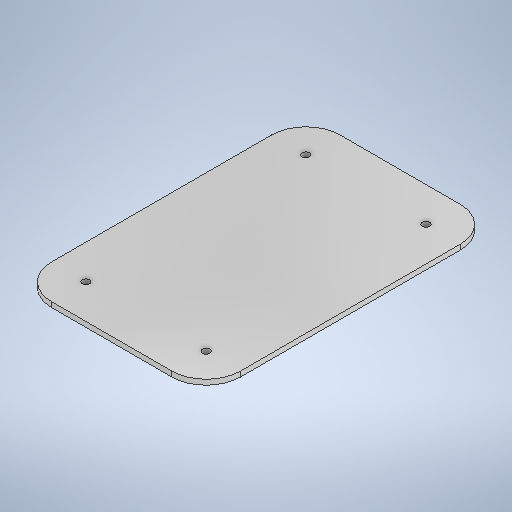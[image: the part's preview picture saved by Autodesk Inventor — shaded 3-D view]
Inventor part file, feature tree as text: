
AUTODESK INVENTOR PART (.ipt)
format: ipt  version: 2025.2 (Build 292293000, 293)  size: 270,848 bytes
history: native  units: mm
features: sketch x2, plane x2, extrude x1, fillet x1, hole x1
ambient origin geometry x8: Origin, YZ Plane, XZ Plane, XY Plane, X Axis, Y Axis, Z Axis, Center Point
bodies: Solid1 (feature_tree)
feature tree (7):
  sketch  "Sketch1"  dims[d4=110.0mm d5=168.0mm d20=3.0mm d21=0.0mm]
  extrude  "Extrusion2"  Depth=168.0mm
  fillet  "Fillet1"  Radius=3.0mm
  plane  "Work Plane1"
  plane  "Work Plane2"
  hole  "Hole2"  [1 undecoded]
  sketch  "Sketch2"  dims[d22=5.0mm d23=18.0mm d24=24.0mm d25=5.0mm d26=18.0mm d27=24.0mm d35=20.0mm d36=-84.0mm d37=-55.0mm d38=4.3mm d39=6.0mm d40=4.0mm d41=2.0mm d42=90.0deg d43=8.0mm d44=20.594885mm]
note: 1 required parameter value undecoded (feature->parameter linkage not recoverable at this tier; creation-order binding heuristic only, values carry confidence <= 0.55)
